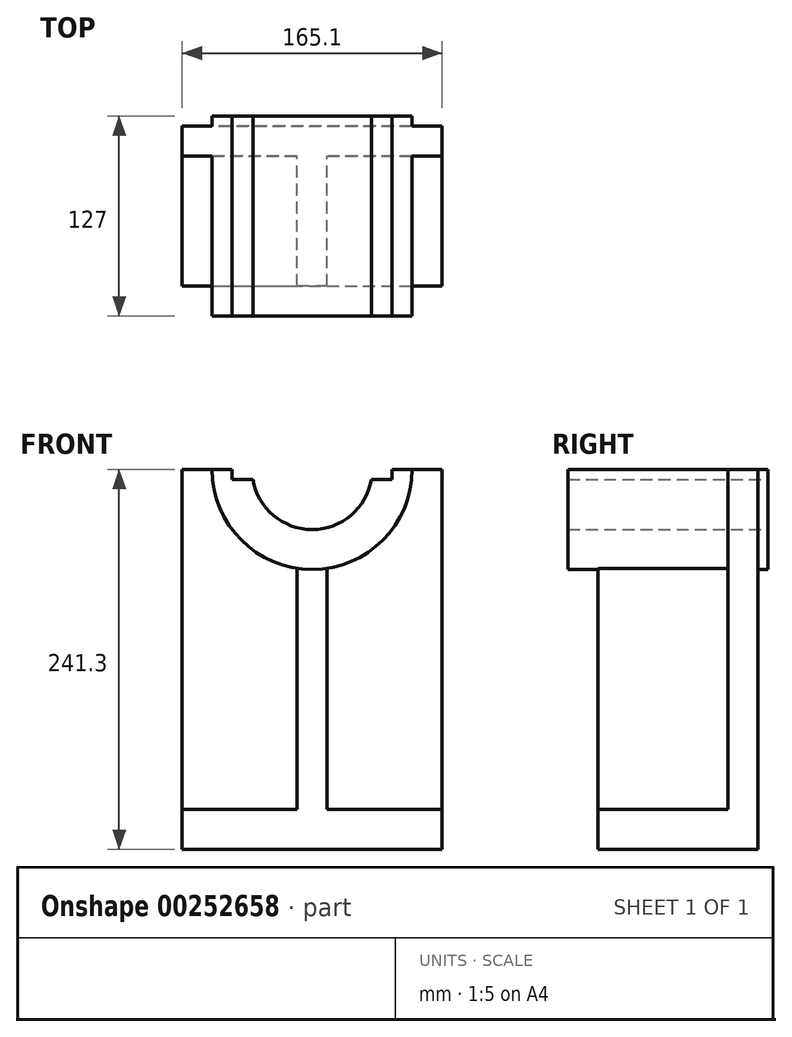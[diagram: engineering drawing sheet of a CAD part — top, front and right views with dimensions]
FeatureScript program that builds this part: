
annotation { "Feature Type Name" : "Feature", "Feature Type Description" : "" }
export const myFeature = defineFeature(function(context is Context, id is Id, definition is map)
    precondition{}
    {
        {
            var Q0;
            Q0=qCreatedBy(makeId("Top.planeOp"),FACE);
            var sketch = newSketch(context, id + "F0", { "sketchPlane" : qUnion([Q0])});
            skLineSegment(sketch, "E0", {"start": v(0, 0) * mm, "end": v(165.1, 0) * mm});
            skLineSegment(sketch, "E1", {"start": v(0, 0) * mm, "end": v(0, 101.6) * mm});
            skLineSegment(sketch, "E2", {"start": v(165.1, 0) * mm, "end": v(165.1, 101.6) * mm});
            skLineSegment(sketch, "E3", {"start": v(0, 101.6) * mm, "end": v(165.1, 101.6) * mm});
            skLineSegment(sketch, "E4", {"start": v(0, 82.55) * mm, "end": v(73.03, 82.55) * mm});
            skLineSegment(sketch, "E5", {"start": v(73.03, 82.55) * mm, "end": v(73.03, 0) * mm});
            skLineSegment(sketch, "E6", {"start": v(92.08, 82.55) * mm, "end": v(92.08, 0) * mm});
            skPoint(sketch, "E7.orphan", {"position": v(73.03, 101.6) * mm});
            skPoint(sketch, "E8.orphan", {"position": v(82.55, 101.6) * mm});
            skPoint(sketch, "E9.orphan", {"position": v(92.08, 101.6) * mm});
            skLineSegment(sketch, "E10.trimOffspring", {"start": v(92.08, 82.55) * mm, "end": v(165.1, 82.55) * mm});
            skPoint(sketch, "E11.start.orphan", {"position": v(82.55, 0) * mm});
            skSolve(sketch);
        }
        {
            var Q0;
            {var subQ0=sQuery(id+"F0.wireOp",EDGE,"E3");Q0=makeQuery(id+"F0.imprint","IMPRINT",FACE,{"disambiguationData":[TD([[makeQuery(id+"F0.imprint","IMPRINT",EDGE,{"derivedFrom":subQ0}),-1.0]])]});}
            extrude(context, id + "F1", {"entities" : qUnion([Q0]), "depth" : 215.9 * mm});
        }
        {
            var Q0;
            {var subQ4=sQuery(id+"F0.wireOp",EDGE,"E4");Q0=makeQuery(id+"F0.imprint","IMPRINT",FACE,{"disambiguationData":[TD([[makeQuery(id+"F0.imprint","IMPRINT",EDGE,{"derivedFrom":subQ4}),-1.0]])]});}
            var Q1;
            Q1=makeQuery(id+"F1.opExtrude","CAP_FACE",FACE,{"disambiguationData":[OSD([sQuery(id+"F0.wireOp",EDGE,"E0"),sQuery(id+"F0.wireOp",EDGE,"E1"),sQuery(id+"F0.wireOp",EDGE,"E2"),sQuery(id+"F0.wireOp",EDGE,"E3"),sQuery(id+"F0.wireOp",EDGE,"E4"),sQuery(id+"F0.wireOp",EDGE,"E5"),sQuery(id+"F0.wireOp",EDGE,"E6"),sQuery(id+"F0.wireOp",EDGE,"E10.trimOffspring")])],"isStart":false});
            var Q2;
            {var subQ3=sQuery(id+"F0.wireOp",EDGE,"E6");Q2=makeQuery(id+"F0.imprint","IMPRINT",FACE,{"disambiguationData":[TD([[makeQuery(id+"F0.imprint","IMPRINT",EDGE,{"derivedFrom":subQ3}),1.0]])]});}
            extrude(context, id + "F2", {"entities" : qUnion([Q0, Q1, Q2]), "operationType" : NewBodyOperationType.ADD, "depth" : 25.4 * mm});
        }
        {
            var Q0;
            {var subQ0=sQuery(id+"F0.wireOp",EDGE,"E3");Q0=makeQuery(id+"F2.boolean.opBoolean","MERGE",FACE,{"derivedFrom":[makeQuery(id+"F1.opExtrude","SWEPT_FACE",FACE,{"disambiguationData":[OSD([subQ0])]}),makeQuery(id+"F2.opExtrude","SWEPT_FACE",FACE,{"disambiguationData":[OSD([subQ0])]})]});}
            var sketch = newSketch(context, id + "F3", { "sketchPlane" : qUnion([Q0])});
            skLineSegment(sketch, "E12", {"start": v(-165.1, 241.3) * mm, "end": v(-82.55, 241.3) * mm});
            skLineSegment(sketch, "E13", {"start": v(-82.55, 241.3) * mm, "end": v(-146.05, 241.3) * mm});
            skArc(sketch, "E14", {"start": v(-146.05, 241.3) * mm, "mid": v(-82.55, 177.8) * mm, "end": v(-19.05, 241.3) * mm});
            skPoint(sketch, "E15", {"position": v(-19.05, 241.3) * mm});
            skPoint(sketch, "E16", {"position": v(-120.65, 241.3) * mm});
            skArc(sketch, "E17", {"start": v(-120.12, 234.95) * mm, "mid": v(-82.55, 203.2) * mm, "end": v(-44.98, 234.95) * mm});
            skPoint(sketch, "E18", {"position": v(-44.45, 241.3) * mm});
            skPoint(sketch, "E19", {"position": v(-133.35, 241.3) * mm});
            skPoint(sketch, "E20", {"position": v(-31.75, 241.3) * mm});
            skLineSegment(sketch, "E21", {"start": v(-133.35, 241.3) * mm, "end": v(-133.35, 234.95) * mm});
            skLineSegment(sketch, "E22", {"start": v(-31.75, 241.3) * mm, "end": v(-31.75, 234.95) * mm});
            skLineSegment(sketch, "E23", {"start": v(-133.35, 234.95) * mm, "end": v(-120.12, 234.95) * mm});
            skLineSegment(sketch, "E24.trimOffspring", {"start": v(-44.98, 234.95) * mm, "end": v(-31.75, 234.95) * mm});
            skSolve(sketch);
        }
        {
            var Q0;
            {var subQ1=sQuery(id+"F3.wireOp",EDGE,"E14");Q0=makeQuery(id+"F3.imprint","IMPRINT",FACE,{"disambiguationData":[TD([[makeQuery(id+"F3.imprint","IMPRINT",EDGE,{"derivedFrom":subQ1}),1.0]])]});}
            extrude(context, id + "F4", {"entities" : qUnion([Q0]), "operationType" : NewBodyOperationType.ADD, "oppositeDirection" : true, "depth" : 120.65 * mm});
        }
        {
            var Q0;
            Q0=makeQuery(id+"F3.imprint","IMPRINT",FACE,{"disambiguationData":[TD([[makeQuery(id+"F3.imprint","IMPRINT",EDGE,{"derivedFrom":sQuery(id+"F3.wireOp",EDGE,"E17")}),1.0]])]});
            extrude(context, id + "F5", {"entities" : qUnion([Q0]), "operationType" : NewBodyOperationType.REMOVE, "oppositeDirection" : true, "depth" : 127 * mm});
        }
        {
            var Q0;
            {var subQ1=sQuery(id+"F3.wireOp",EDGE,"E14");Q0=makeQuery(id+"F3.imprint","IMPRINT",FACE,{"disambiguationData":[TD([[makeQuery(id+"F3.imprint","IMPRINT",EDGE,{"derivedFrom":subQ1}),1.0]])]});}
            extrude(context, id + "F6", {"entities" : qUnion([Q0]), "operationType" : NewBodyOperationType.ADD, "depth" : 6.35 * mm});
        }
    });
